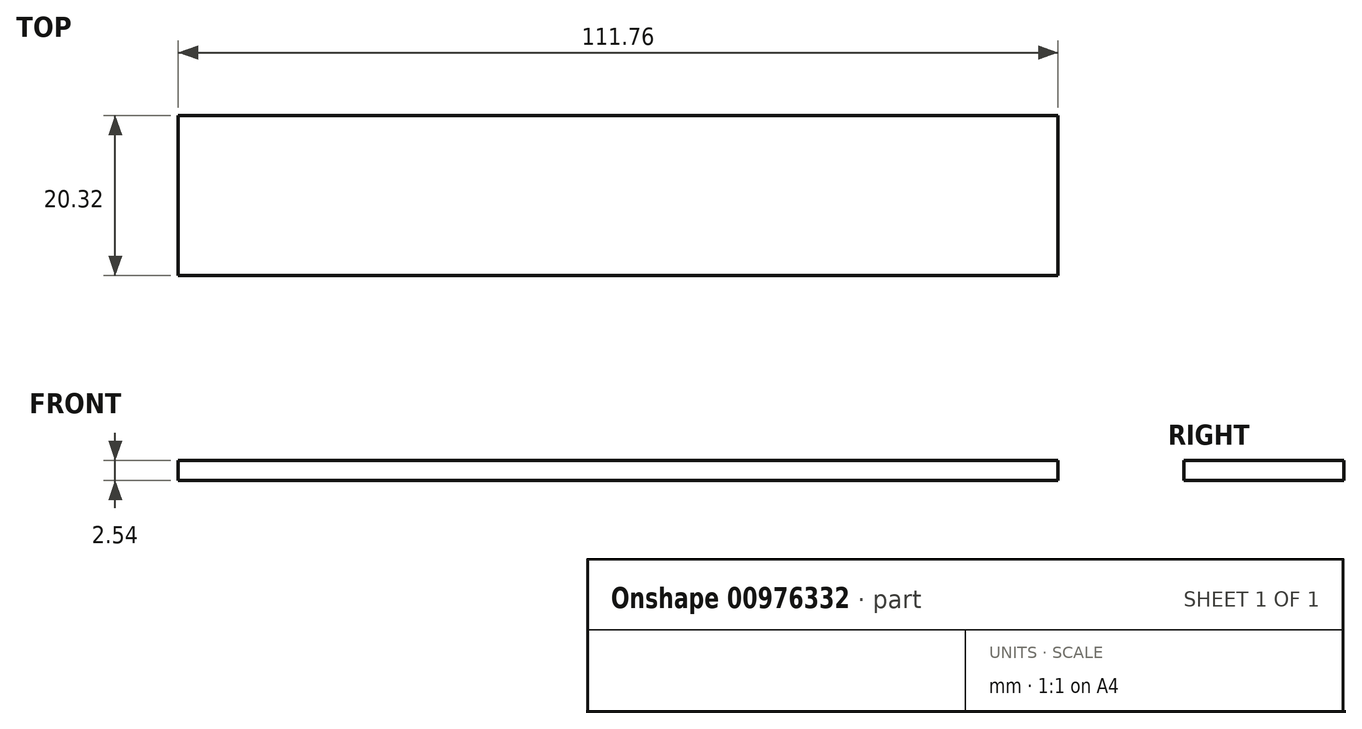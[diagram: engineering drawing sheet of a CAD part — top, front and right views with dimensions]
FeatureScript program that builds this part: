
annotation { "Feature Type Name" : "Feature", "Feature Type Description" : "" }
export const myFeature = defineFeature(function(context is Context, id is Id, definition is map)
    precondition{}
    {
        {
            var Q0;
            Q0=qCreatedBy(makeId("Top.planeOp"),FACE);
            var sketch = newSketch(context, id + "F0", { "sketchPlane" : qUnion([Q0])});
            skLineSegment(sketch, "E0.bottom", {"start": v(-55.88, 10.16) * mm, "end": v(55.88, 10.16) * mm});
            skLineSegment(sketch, "E0.top", {"start": v(-55.88, -10.16) * mm, "end": v(55.88, -10.16) * mm});
            skLineSegment(sketch, "E0.left", {"start": v(-55.88, 10.16) * mm, "end": v(-55.88, -10.16) * mm});
            skLineSegment(sketch, "E0.right", {"start": v(55.88, 10.16) * mm, "end": v(55.88, -10.16) * mm});
            skPoint(sketch, "E0.middle", {"position": v(0, 0) * mm});
            skSolve(sketch);
        }
        {
            var Q0;
            Q0=makeQuery(id+"F0.imprint","IMPRINT",FACE,{"disambiguationData":[TD([[makeQuery(id+"F0.imprint","IMPRINT",EDGE,{"derivedFrom":sQuery(id+"F0.wireOp",EDGE,"E0.bottom")}),-1.0]])]});
            extrude(context, id + "F1", {"entities" : qUnion([Q0]), "depth" : 2.54 * mm, "offsetDistance" : 25.4 * mm});
        }
    });
